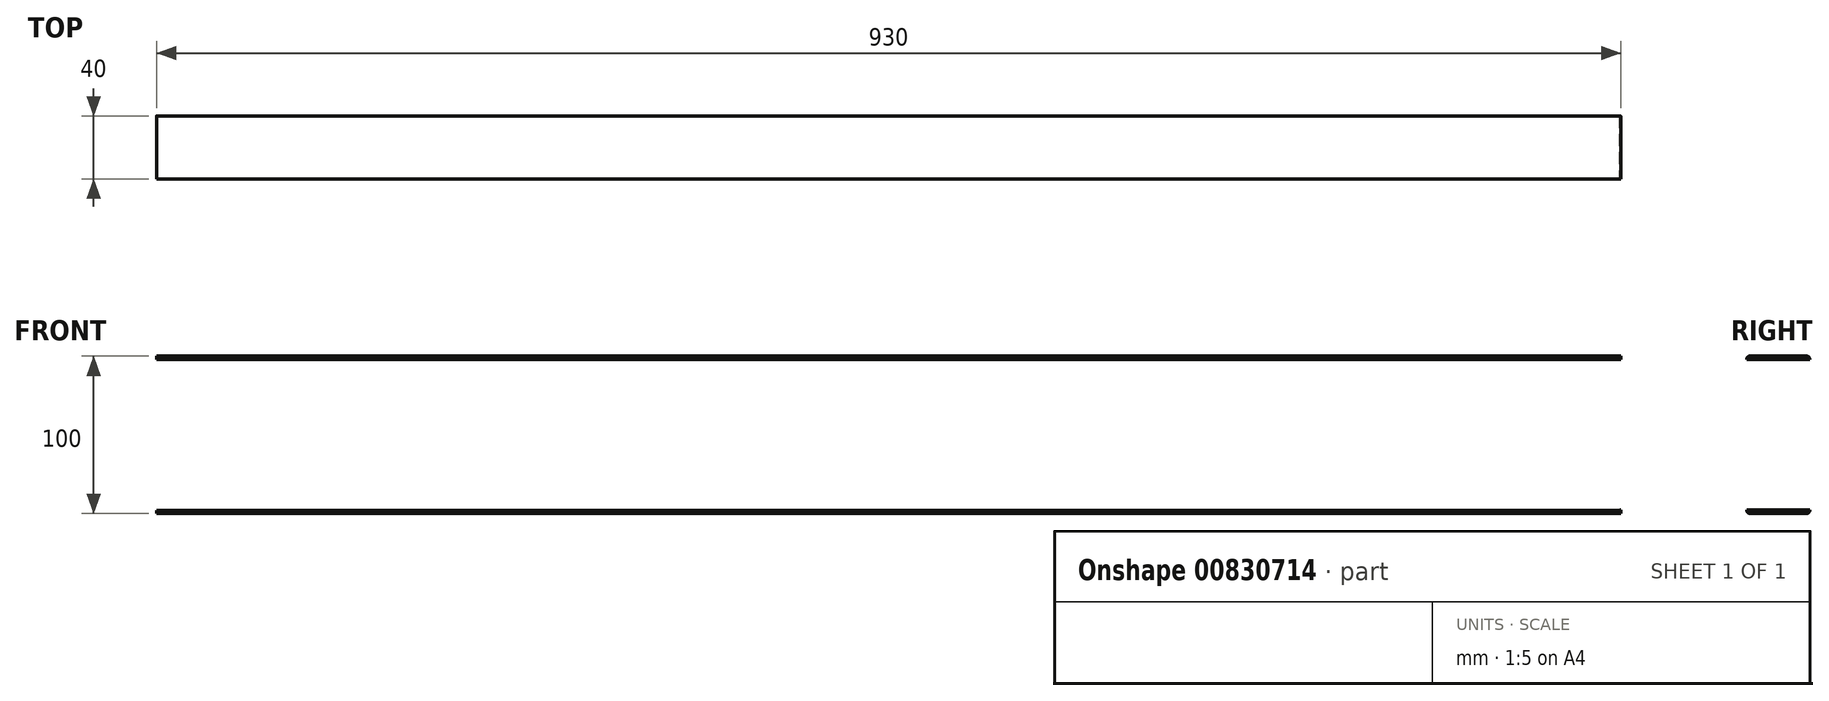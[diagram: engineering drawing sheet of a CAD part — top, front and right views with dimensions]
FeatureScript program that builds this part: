
annotation { "Feature Type Name" : "Feature", "Feature Type Description" : "" }
export const myFeature = defineFeature(function(context is Context, id is Id, definition is map)
    precondition{}
    {
        {
            assignVariable(context, id + "F0", {"name" : "TubeHeight", "anyValue" : 40});
        }
        {
            assignVariable(context, id + "F1", {"name" : "TubeWidth", "anyValue" : 100});
        }
        {
            assignVariable(context, id + "F2", {"name" : "ScissorLength", "anyValue" : 1000});
        }
        {
            var Q0;
            Q0=qCreatedBy(makeId("Right.planeOp"),FACE);
            var sketch = newSketch(context, id + "F3", { "sketchPlane" : qUnion([Q0])});
            skPoint(sketch, "E0.middle", {"position": v(0, 0) * mm});
            skLineSegment(sketch, "E1.bottom", {"start": v(-2.3, -86.5) * mm, "end": v(33.7, -86.5) * mm});
            skLineSegment(sketch, "E1.top", {"start": v(-2.3, 13.5) * mm, "end": v(33.7, 13.5) * mm});
            skLineSegment(sketch, "E1.left", {"start": v(-4.3, -84.5) * mm, "end": v(-4.3, 11.5) * mm});
            skLineSegment(sketch, "E1.right", {"start": v(35.7, -84.5) * mm, "end": v(35.7, 11.5) * mm});
            skPoint(sketch, "E2.visualSharp", {"position": v(-4.3, 13.5) * mm});
            skArc(sketch, "E2.filletArc", {"start": v(-2.3, 13.5) * mm, "mid": v(-3.7, 12.91) * mm, "end": v(-4.3, 11.5) * mm});
            skPoint(sketch, "E3.visualSharp", {"position": v(35.7, 13.5) * mm});
            skArc(sketch, "E3.filletArc", {"start": v(35.7, 11.5) * mm, "mid": v(35.12, 12.91) * mm, "end": v(33.7, 13.5) * mm});
            skPoint(sketch, "E4.visualSharp", {"position": v(35.7, -86.5) * mm});
            skArc(sketch, "E4.filletArc", {"start": v(33.7, -86.5) * mm, "mid": v(35.12, -85.91) * mm, "end": v(35.7, -84.5) * mm});
            skPoint(sketch, "E5.visualSharp", {"position": v(-4.3, -86.5) * mm});
            skArc(sketch, "E5.filletArc", {"start": v(-4.3, -84.5) * mm, "mid": v(-3.7, -85.91) * mm, "end": v(-2.3, -86.5) * mm});
            skLineSegment(sketch, "E6.0", {"start": v(-2.3, 11.5) * mm, "end": v(-2.3, 11.5) * mm});
            skLineSegment(sketch, "E6.2", {"start": v(-2.3, -84.5) * mm, "end": v(-2.3, -84.5) * mm});
            skLineSegment(sketch, "E6.4", {"start": v(33.7, -84.5) * mm, "end": v(33.7, -84.5) * mm});
            skLineSegment(sketch, "E6.7", {"start": v(33.7, 11.5) * mm, "end": v(33.7, 11.5) * mm});
            skLineSegment(sketch, "E7.0", {"start": v(25.7, -76.5) * mm, "end": v(25.7, 3.5) * mm});
            skLineSegment(sketch, "E7.1", {"start": v(5.7, -76.5) * mm, "end": v(25.7, -76.5) * mm});
            skLineSegment(sketch, "E7.2", {"start": v(5.7, -76.5) * mm, "end": v(5.7, 3.5) * mm});
            skLineSegment(sketch, "E7.3", {"start": v(5.7, 3.5) * mm, "end": v(25.7, 3.5) * mm});
            skSolve(sketch);
        }
        {
            var Q0;
            Q0=makeQuery(id+"F3.imprint","IMPRINT",FACE,{"disambiguationData":[TD([[makeQuery(id+"F3.imprint","IMPRINT",EDGE,{"derivedFrom":sQuery(id+"F3.wireOp",EDGE,"E1.bottom")}),1.0]])]});
            extrude(context, id + "F4", {"entities" : qUnion([Q0]), "endBound" : BoundingType.SYMMETRIC, "depth" : (getVariable(context, 'ScissorLength')) * mm, "hasOffset" : true, "offsetDistance" : 1000 * mm});
        }
        {
            var Q0;
            Q0=makeQuery(id+"F4.opExtrude","SWEPT_FACE",FACE,{"disambiguationData":[OSD([sQuery(id+"F3.wireOp",EDGE,"E1.left")])]});
            var sketch = newSketch(context, id + "F5", { "sketchPlane" : qUnion([Q0])});
            skPoint(sketch, "E8", {"position": v(0, -36.22) * mm});
            skPoint(sketch, "E9.centerSnap0", {"position": v(500, -36.5) * mm});
            skCircle(sketch, "E10.MirrorC", {"center": v(450, -36.22) * mm, "radius": 16.43 * mm, "construction": true});
            skPoint(sketch, "E11.centerSnap0", {"position": v(-500, -36.5) * mm});
            skArc(sketch, "E12", {"start": v(-453.18, 13.4) * mm, "mid": v(-499.97, -38.34) * mm, "end": v(-449.5, -86.5) * mm});
            skPoint(sketch, "E12.second.point", {"position": v(-400, -36.5) * mm});
            skPoint(sketch, "E12.third.point", {"position": v(-453.18, 13.4) * mm});
            skPoint(sketch, "E13", {"position": v(-449.5, -86.5) * mm});
            skArc(sketch, "E14.MirrorCS", {"start": v(453.18, 13.4) * mm, "mid": v(499.97, -38.34) * mm, "end": v(449.5, -86.5) * mm});
            skSolve(sketch);
        }
        {
            var Q0;
            Q0=sQuery(id+"F5.wireOp",VERTEX,"gL0Hj35o-Ipak-IrFQ-axua-rWeWUbhPRuIx.center");
            var Q1;
            Q1=sQuery(id+"F5.wireOp",VERTEX,"E10.MirrorC.center");
            var Q2;
            Q2=sQuery(id+"F5.wireOp",VERTEX,"E8");
            var Q3;
            Q3=sQuery(id+"F5.wireOp",VERTEX,"E12.center");
            var Q4;
            Q4=makeQuery(id+"F4.opExtrude","SWEPT_BODY",BODY,{"disambiguationData":[OSD([sQuery(id+"F3.wireOp",EDGE,"E1.bottom"),sQuery(id+"F3.wireOp",EDGE,"E1.top"),sQuery(id+"F3.wireOp",EDGE,"E1.left"),sQuery(id+"F3.wireOp",EDGE,"E1.right"),sQuery(id+"F3.wireOp",EDGE,"E2.filletArc"),sQuery(id+"F3.wireOp",EDGE,"E3.filletArc"),sQuery(id+"F3.wireOp",EDGE,"E4.filletArc"),sQuery(id+"F3.wireOp",EDGE,"E5.filletArc"),sQuery(id+"F3.wireOp",EDGE,"E7.0"),sQuery(id+"F3.wireOp",EDGE,"E7.1"),sQuery(id+"F3.wireOp",EDGE,"E7.2"),sQuery(id+"F3.wireOp",EDGE,"E7.3")])]});
            hole(context, id + "F6", {"style" : HoleStyle.SIMPLE, "endStyle" : HoleEndStyle.BLIND, "standardTappedOrClearance" : lookupTablePath({ "fit" : "Normal", "standard" : "ISO", "size" : "M16", "type" : "Clearance" }), "standardBlindInLast" : lookupTablePath({ "fit" : "Standard", "standard" : "ISO", "size" : "M16", "type" : "Clearance" }), "holeDiameter" : 17.5 * mm, "majorDiameter" : 5 * mm, "holeDepth" : 40 * mm, "isTappedThrough" : true, "tappedDepth" : 12 * mm, "tapClearance" : 3, "startFromSketch" : true, "locations" : qUnion([Q0, Q1, Q2, Q3]), "scope" : qUnion([Q4])});
        }
        {
            var Q0;
            {var subQ0=sQuery(id+"F5.wireOp",EDGE,"E12");var subQ1=sQuery(id+"F3.wireOp",EDGE,"E1.left");var subQ4=makeQuery(id+"F4.opExtrude","CAP_EDGE",EDGE,{"disambiguationData":[OSD([subQ1])],"isStart":true});var subQ5=makeQuery(id+"F5.imprint","INTERSECT",VERTEX,{"derivedFrom":[subQ4,subQ0]});Q0=makeQuery(id+"F5.imprint","IMPRINT",FACE,{"disambiguationData":[TD([[makeQuery(id+"F5.imprint","IMPRINT",EDGE,{"disambiguationData":[TD([[subQ5,1.0]])],"derivedFrom":subQ0}),-1.0]])]});}
            var Q1;
            {var subQ0=sQuery(id+"F5.wireOp",EDGE,"E12");var subQ1=sQuery(id+"F3.wireOp",EDGE,"E1.left");var subQ2=makeQuery(id+"F4.opExtrude","CAP_EDGE",EDGE,{"disambiguationData":[OSD([subQ1])],"isStart":true});var subQ3=makeQuery(id+"F5.imprint","INTERSECT",VERTEX,{"derivedFrom":[subQ2,subQ0]});Q1=makeQuery(id+"F5.imprint","IMPRINT",FACE,{"disambiguationData":[TD([[makeQuery(id+"F5.imprint","IMPRINT",EDGE,{"disambiguationData":[TD([[subQ3,-1.0]])],"derivedFrom":subQ0}),-1.0]])]});}
            var Q2;
            {var subQ0=sQuery(id+"F5.wireOp",EDGE,"E14.MirrorCS");var subQ1=sQuery(id+"F3.wireOp",EDGE,"E1.left");var subQ4=makeQuery(id+"F4.opExtrude","CAP_EDGE",EDGE,{"disambiguationData":[OSD([subQ1])],"isStart":false});var subQ5=makeQuery(id+"F5.imprint","INTERSECT",VERTEX,{"derivedFrom":[subQ4,subQ0]});Q2=makeQuery(id+"F5.imprint","IMPRINT",FACE,{"disambiguationData":[TD([[makeQuery(id+"F5.imprint","IMPRINT",EDGE,{"disambiguationData":[TD([[subQ5,1.0]])],"derivedFrom":subQ0}),1.0]])]});}
            var Q3;
            {var subQ0=sQuery(id+"F5.wireOp",EDGE,"E14.MirrorCS");var subQ1=sQuery(id+"F3.wireOp",EDGE,"E1.left");var subQ4=makeQuery(id+"F4.opExtrude","CAP_EDGE",EDGE,{"disambiguationData":[OSD([subQ1])],"isStart":false});var subQ5=makeQuery(id+"F5.imprint","INTERSECT",VERTEX,{"derivedFrom":[subQ4,subQ0]});Q3=makeQuery(id+"F5.imprint","IMPRINT",FACE,{"disambiguationData":[TD([[makeQuery(id+"F5.imprint","IMPRINT",EDGE,{"disambiguationData":[TD([[subQ5,-1.0]])],"derivedFrom":subQ0}),1.0]])]});}
            var Q4;
            Q4=sQuery(id+"F5.wireOp",EDGE,"giCMITpL-clwF-rWN8-tJVd-up4GtD5okeqH");
            extrude(context, id + "F7", {"entities" : qUnion([Q0, Q1, Q2, Q3]), "operationType" : NewBodyOperationType.REMOVE, "surfaceEntities" : qUnion([Q4]), "depth" : -(getVariable(context, 'TubeHeight')) * mm, "offsetDistance" : 25 * mm});
        }
        {
            var Q0;
            {var subQ0=sQuery(id+"F3.wireOp",EDGE,"E1.top");var subQ1=sQuery(id+"F3.wireOp",EDGE,"E2.filletArc");var subQ2=sQuery(id+"F3.wireOp",EDGE,"E1.left");var subQ3=sQuery(id+"F3.wireOp",EDGE,"E3.filletArc");Q0=makeQuery(id+"F7.boolean.opBoolean","SPLIT",FACE,{"disambiguationData":[TD([makeQuery(id+"F4.opExtrude","SWEPT_FACE",FACE,{"disambiguationData":[OSD([subQ0])]})])],"derivedFrom":makeQuery(id+"F4.opExtrude","CAP_FACE",FACE,{"disambiguationData":[OSD([sQuery(id+"F3.wireOp",EDGE,"E1.bottom"),subQ0,subQ2,sQuery(id+"F3.wireOp",EDGE,"E1.right"),subQ1,subQ3,sQuery(id+"F3.wireOp",EDGE,"E4.filletArc"),sQuery(id+"F3.wireOp",EDGE,"E5.filletArc"),sQuery(id+"F3.wireOp",EDGE,"E7.0"),sQuery(id+"F3.wireOp",EDGE,"E7.1"),sQuery(id+"F3.wireOp",EDGE,"E7.2"),sQuery(id+"F3.wireOp",EDGE,"E7.3")])],"isStart":true})});}
            var Q1;
            {var subQ0=sQuery(id+"F3.wireOp",EDGE,"E1.bottom");var subQ1=sQuery(id+"F3.wireOp",EDGE,"E4.filletArc");var subQ2=sQuery(id+"F3.wireOp",EDGE,"E5.filletArc");var subQ3=sQuery(id+"F3.wireOp",EDGE,"E1.left");Q1=makeQuery(id+"F7.boolean.opBoolean","SPLIT",FACE,{"disambiguationData":[TD([makeQuery(id+"F4.opExtrude","SWEPT_FACE",FACE,{"disambiguationData":[OSD([subQ0])]})])],"derivedFrom":makeQuery(id+"F4.opExtrude","CAP_FACE",FACE,{"disambiguationData":[OSD([subQ0,sQuery(id+"F3.wireOp",EDGE,"E1.top"),subQ3,sQuery(id+"F3.wireOp",EDGE,"E1.right"),sQuery(id+"F3.wireOp",EDGE,"E2.filletArc"),sQuery(id+"F3.wireOp",EDGE,"E3.filletArc"),subQ1,subQ2,sQuery(id+"F3.wireOp",EDGE,"E7.0"),sQuery(id+"F3.wireOp",EDGE,"E7.1"),sQuery(id+"F3.wireOp",EDGE,"E7.2"),sQuery(id+"F3.wireOp",EDGE,"E7.3")])],"isStart":true})});}
            var Q2;
            Q2=sQuery(id+"F3.wireOp",EDGE,"E3.filletArc");
            var Q3;
            Q3=sQuery(id+"F3.wireOp",EDGE,"E1.top");
            var Q4;
            Q4=sQuery(id+"F3.wireOp",EDGE,"E2.filletArc");
            extrude(context, id + "F8", {"entities" : qUnion([Q0, Q1]), "operationType" : NewBodyOperationType.REMOVE, "surfaceEntities" : qUnion([Q2, Q3, Q4]), "oppositeDirection" : true, "depth" : (getVariable(context, 'TubeWidth') / 2 - 15) * mm, "offsetDistance" : 25 * mm});
        }
        {
            var Q0;
            {var subQ0=sQuery(id+"F3.wireOp",EDGE,"E1.bottom");var subQ1=sQuery(id+"F3.wireOp",EDGE,"E4.filletArc");var subQ2=sQuery(id+"F3.wireOp",EDGE,"E5.filletArc");var subQ3=sQuery(id+"F3.wireOp",EDGE,"E1.left");Q0=makeQuery(id+"F7.boolean.opBoolean","SPLIT",FACE,{"disambiguationData":[TD([makeQuery(id+"F4.opExtrude","SWEPT_FACE",FACE,{"disambiguationData":[OSD([subQ0])]})])],"derivedFrom":makeQuery(id+"F4.opExtrude","CAP_FACE",FACE,{"disambiguationData":[OSD([subQ0,sQuery(id+"F3.wireOp",EDGE,"E1.top"),subQ3,sQuery(id+"F3.wireOp",EDGE,"E1.right"),sQuery(id+"F3.wireOp",EDGE,"E2.filletArc"),sQuery(id+"F3.wireOp",EDGE,"E3.filletArc"),subQ1,subQ2,sQuery(id+"F3.wireOp",EDGE,"E7.0"),sQuery(id+"F3.wireOp",EDGE,"E7.1"),sQuery(id+"F3.wireOp",EDGE,"E7.2"),sQuery(id+"F3.wireOp",EDGE,"E7.3")])],"isStart":false})});}
            var Q1;
            {var subQ0=sQuery(id+"F3.wireOp",EDGE,"E1.top");var subQ1=sQuery(id+"F3.wireOp",EDGE,"E2.filletArc");var subQ2=sQuery(id+"F3.wireOp",EDGE,"E1.left");var subQ4=sQuery(id+"F3.wireOp",EDGE,"E3.filletArc");Q1=makeQuery(id+"F7.boolean.opBoolean","SPLIT",FACE,{"disambiguationData":[TD([makeQuery(id+"F4.opExtrude","SWEPT_FACE",FACE,{"disambiguationData":[OSD([subQ0])]})])],"derivedFrom":makeQuery(id+"F4.opExtrude","CAP_FACE",FACE,{"disambiguationData":[OSD([sQuery(id+"F3.wireOp",EDGE,"E1.bottom"),subQ0,subQ2,sQuery(id+"F3.wireOp",EDGE,"E1.right"),subQ1,subQ4,sQuery(id+"F3.wireOp",EDGE,"E4.filletArc"),sQuery(id+"F3.wireOp",EDGE,"E5.filletArc"),sQuery(id+"F3.wireOp",EDGE,"E7.0"),sQuery(id+"F3.wireOp",EDGE,"E7.1"),sQuery(id+"F3.wireOp",EDGE,"E7.2"),sQuery(id+"F3.wireOp",EDGE,"E7.3")])],"isStart":false})});}
            extrude(context, id + "F9", {"entities" : qUnion([Q0, Q1]), "operationType" : NewBodyOperationType.REMOVE, "oppositeDirection" : true, "depth" : (getVariable(context, 'TubeWidth') / 2 - 15) * mm, "offsetDistance" : 25 * mm});
        }
    });
